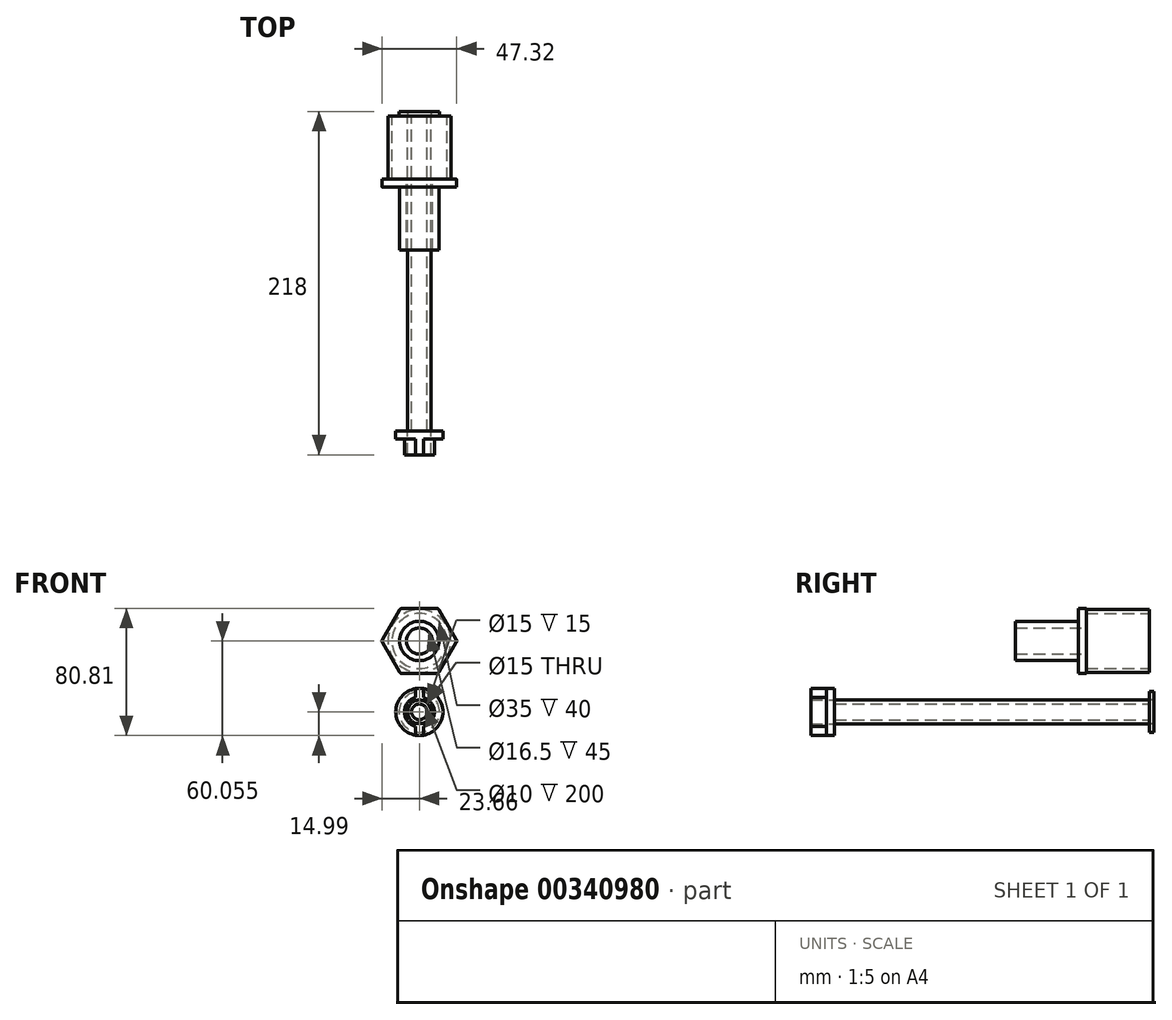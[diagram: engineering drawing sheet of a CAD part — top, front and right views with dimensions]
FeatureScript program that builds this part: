
annotation { "Feature Type Name" : "Feature", "Feature Type Description" : "" }
export const myFeature = defineFeature(function(context is Context, id is Id, definition is map)
    precondition{}
    {
        {
            var Q0;
            Q0=qCreatedBy(makeId("Front.planeOp"),FACE);
            var sketch = newSketch(context, id + "F0", { "sketchPlane" : qUnion([Q0])});
            skCircle(sketch, "E0", {"center": v(0, 0) * mm, "radius": 7.5 * mm});
            skCircle(sketch, "E1", {"center": v(0, 0) * mm, "radius": 5 * mm});
            skSolve(sketch);
        }
        {
            var Q0;
            Q0=makeQuery(id+"F0.imprint","IMPRINT",FACE,{"disambiguationData":[TD([[makeQuery(id+"F0.imprint","IMPRINT",EDGE,{"derivedFrom":sQuery(id+"F0.wireOp",EDGE,"E0")}),1.0]])]});
            extrude(context, id + "F1", {"entities" : qUnion([Q0]), "depth" : 200 * mm});
        }
        {
            var Q0;
            Q0=makeQuery(id+"F1.opExtrude","CAP_FACE",FACE,{"disambiguationData":[OSD([sQuery(id+"F0.wireOp",EDGE,"E0"),sQuery(id+"F0.wireOp",EDGE,"E1")])],"isStart":false});
            var sketch = newSketch(context, id + "F2", { "sketchPlane" : qUnion([Q0])});
            skCircle(sketch, "E2", {"center": v(0, 0) * mm, "radius": 7.5 * mm});
            skCircle(sketch, "E3", {"center": v(0, 0) * mm, "radius": 14.99 * mm});
            skSolve(sketch);
        }
        {
            var Q0;
            Q0=makeQuery(id+"F2.imprint","IMPRINT",FACE,{"disambiguationData":[TD([[makeQuery(id+"F2.imprint","IMPRINT",EDGE,{"derivedFrom":sQuery(id+"F2.wireOp",EDGE,"E2")}),-1.0]])]});
            extrude(context, id + "F3", {"entities" : qUnion([Q0]), "depth" : 5 * mm});
        }
        {
            var Q0;
            Q0=makeQuery(id+"F3.opExtrude","CAP_FACE",FACE,{"disambiguationData":[OSD([sQuery(id+"F2.wireOp",EDGE,"E2"),sQuery(id+"F2.wireOp",EDGE,"E3")])],"isStart":false});
            var sketch = newSketch(context, id + "F4", { "sketchPlane" : qUnion([Q0])});
            skCircle(sketch, "E4", {"center": v(0, 0) * mm, "radius": 14.99 * mm});
            skCircle(sketch, "E5", {"center": v(0, 0) * mm, "radius": 7.5 * mm});
            skCircle(sketch, "E6", {"center": v(0, 0) * mm, "radius": 9.5 * mm});
            skLineSegment(sketch, "E7", {"start": v(-2.5, 9.17) * mm, "end": v(-2.5, 14.78) * mm});
            skLineSegment(sketch, "E8", {"start": v(2.5, 9.17) * mm, "end": v(2.5, 14.78) * mm});
            skLineSegment(sketch, "E9", {"start": v(2.5, -9.17) * mm, "end": v(2.5, -14.78) * mm});
            skLineSegment(sketch, "E10", {"start": v(-2.5, -9.17) * mm, "end": v(-2.5, -14.78) * mm});
            skLineSegment(sketch, "E11", {"start": v(-2.5, 11.97) * mm, "end": v(0, 11.97) * mm, "construction": true});
            skLineSegment(sketch, "E12", {"start": v(0, 11.97) * mm, "end": v(2.5, 11.97) * mm, "construction": true});
            skLineSegment(sketch, "E13", {"start": v(-2.5, -11.97) * mm, "end": v(0, -11.97) * mm, "construction": true});
            skLineSegment(sketch, "E14", {"start": v(0, -11.97) * mm, "end": v(2.5, -11.97) * mm, "construction": true});
            skLineSegment(sketch, "E15", {"start": v(-2.5, -9.17) * mm, "end": v(-2.5, 9.17) * mm, "construction": true});
            skSolve(sketch);
        }
        {
            var Q0;
            {var subQ0=sQuery(id+"F4.wireOp",EDGE,"E7");Q0=makeQuery(id+"F4.imprint","IMPRINT",FACE,{"disambiguationData":[TD([[makeQuery(id+"F4.imprint","IMPRINT",EDGE,{"derivedFrom":subQ0}),-1.0]])]});}
            var Q1;
            {var subQ0=sQuery(id+"F4.wireOp",EDGE,"E9");Q1=makeQuery(id+"F4.imprint","IMPRINT",FACE,{"disambiguationData":[TD([[makeQuery(id+"F4.imprint","IMPRINT",EDGE,{"derivedFrom":subQ0}),-1.0]])]});}
            var Q2;
            Q2=makeQuery(id+"F4.imprint","IMPRINT",FACE,{"disambiguationData":[TD([[makeQuery(id+"F4.imprint","IMPRINT",EDGE,{"derivedFrom":sQuery(id+"F4.wireOp",EDGE,"E5")}),-1.0]])]});
            extrude(context, id + "F5", {"entities" : qUnion([Q0, Q1, Q2]), "operationType" : NewBodyOperationType.ADD, "depth" : 10 * mm});
        }
        {
            var Q0;
            Q0=qCreatedBy(makeId("Front.planeOp"),FACE);
            var sketch = newSketch(context, id + "F6", { "sketchPlane" : qUnion([Q0])});
            skCircle(sketch, "E16", {"center": v(0, 45.07) * mm, "radius": 17.5 * mm});
            skCircle(sketch, "E17", {"center": v(0, 45.07) * mm, "radius": 20 * mm});
            skSolve(sketch);
        }
        {
            var Q0;
            Q0 = qSketchRegion(id + "F6", true);
            extrude(context, id + "F7", {"entities" : qUnion([Q0]), "depth" : 40 * mm});
        }
        {
            var Q0;
            Q0=makeQuery(id+"F7.opExtrude","CAP_FACE",FACE,{"disambiguationData":[OSD([sQuery(id+"F6.wireOp",EDGE,"E16"),sQuery(id+"F6.wireOp",EDGE,"E17")])],"isStart":false});
            var sketch = newSketch(context, id + "F8", { "sketchPlane" : qUnion([Q0])});
            skCircle(sketch, "E18.cCircle", {"center": v(0, 45.07) * mm, "radius": 20.76 * mm, "construction": true});
            skLineSegment(sketch, "E18.0", {"start": v(-10.83, 65.82) * mm, "end": v(10.83, 65.82) * mm});
            skLineSegment(sketch, "E18.1", {"start": v(12.56, 64.82) * mm, "end": v(23.4, 46.07) * mm});
            skLineSegment(sketch, "E18.2", {"start": v(23.4, 44.07) * mm, "end": v(12.56, 25.3) * mm});
            skLineSegment(sketch, "E18.3", {"start": v(10.83, 24.3) * mm, "end": v(-10.83, 24.3) * mm});
            skLineSegment(sketch, "E18.4", {"start": v(-12.56, 25.3) * mm, "end": v(-23.4, 44.07) * mm});
            skLineSegment(sketch, "E18.5", {"start": v(-23.4, 46.07) * mm, "end": v(-12.56, 64.82) * mm});
            skPoint(sketch, "E18.0.midPoint", {"position": v(0, 65.82) * mm});
            skCircle(sketch, "E19", {"center": v(0, 45.07) * mm, "radius": 8.25 * mm});
            skPoint(sketch, "E20.visualSharp", {"position": v(-23.97, 45.07) * mm});
            skArc(sketch, "E20.filletArc", {"start": v(-23.4, 46.07) * mm, "mid": v(-23.66, 45.07) * mm, "end": v(-23.4, 44.07) * mm});
            skPoint(sketch, "E21.visualSharp", {"position": v(-11.98, 24.3) * mm});
            skArc(sketch, "E21.filletArc", {"start": v(-12.56, 25.3) * mm, "mid": v(-11.83, 24.58) * mm, "end": v(-10.83, 24.3) * mm});
            skPoint(sketch, "E22.visualSharp", {"position": v(11.98, 24.3) * mm});
            skArc(sketch, "E22.filletArc", {"start": v(10.83, 24.3) * mm, "mid": v(11.83, 24.58) * mm, "end": v(12.56, 25.3) * mm});
            skPoint(sketch, "E23.visualSharp", {"position": v(23.97, 45.07) * mm});
            skArc(sketch, "E23.filletArc", {"start": v(23.4, 44.07) * mm, "mid": v(23.66, 45.07) * mm, "end": v(23.4, 46.07) * mm});
            skPoint(sketch, "E24.visualSharp", {"position": v(11.98, 65.82) * mm});
            skArc(sketch, "E24.filletArc", {"start": v(12.56, 64.82) * mm, "mid": v(11.83, 65.55) * mm, "end": v(10.83, 65.82) * mm});
            skPoint(sketch, "E25.visualSharp", {"position": v(-11.98, 65.82) * mm});
            skArc(sketch, "E25.filletArc", {"start": v(-10.83, 65.82) * mm, "mid": v(-11.83, 65.55) * mm, "end": v(-12.56, 64.82) * mm});
            skSolve(sketch);
        }
        {
            var Q0;
            Q0 = qSketchRegion(id + "F8", true);
            extrude(context, id + "F9", {"entities" : qUnion([Q0]), "operationType" : NewBodyOperationType.ADD, "depth" : 5 * mm});
        }
        {
            var Q0;
            Q0=makeQuery(id+"F9.opExtrude","CAP_FACE",FACE,{"disambiguationData":[OSD([sQuery(id+"F8.wireOp",EDGE,"E18.0"),sQuery(id+"F8.wireOp",EDGE,"E18.1"),sQuery(id+"F8.wireOp",EDGE,"E18.2"),sQuery(id+"F8.wireOp",EDGE,"E18.3"),sQuery(id+"F8.wireOp",EDGE,"E18.4"),sQuery(id+"F8.wireOp",EDGE,"E18.5"),sQuery(id+"F8.wireOp",EDGE,"E19"),sQuery(id+"F8.wireOp",EDGE,"E20.filletArc"),sQuery(id+"F8.wireOp",EDGE,"E21.filletArc"),sQuery(id+"F8.wireOp",EDGE,"E22.filletArc"),sQuery(id+"F8.wireOp",EDGE,"E23.filletArc"),sQuery(id+"F8.wireOp",EDGE,"E24.filletArc"),sQuery(id+"F8.wireOp",EDGE,"E25.filletArc")])],"isStart":false});
            var sketch = newSketch(context, id + "F10", { "sketchPlane" : qUnion([Q0])});
            skCircle(sketch, "E26", {"center": v(0, 45.07) * mm, "radius": 8.25 * mm});
            skCircle(sketch, "E27", {"center": v(0, 45.07) * mm, "radius": 12.5 * mm});
            skSolve(sketch);
        }
        {
            var Q0;
            Q0 = qSketchRegion(id + "F10", true);
            extrude(context, id + "F11", {"entities" : qUnion([Q0]), "operationType" : NewBodyOperationType.ADD, "depth" : 40 * mm});
        }
        {
            var Q0;
            Q0=makeQuery(id+"F1.opExtrude","CAP_FACE",FACE,{"disambiguationData":[OSD([sQuery(id+"F0.wireOp",EDGE,"E0"),sQuery(id+"F0.wireOp",EDGE,"E1")])],"isStart":true});
            var sketch = newSketch(context, id + "F12", { "sketchPlane" : qUnion([Q0])});
            skCircle(sketch, "E28", {"center": v(0, 0) * mm, "radius": 7.5 * mm});
            skCircle(sketch, "E29", {"center": v(0, 0) * mm, "radius": 12.87 * mm});
            skSolve(sketch);
        }
        {
            var Q0;
            Q0 = qSketchRegion(id + "F12", true);
            extrude(context, id + "F13", {"entities" : qUnion([Q0]), "depth" : 3 * mm});
        }
    });
